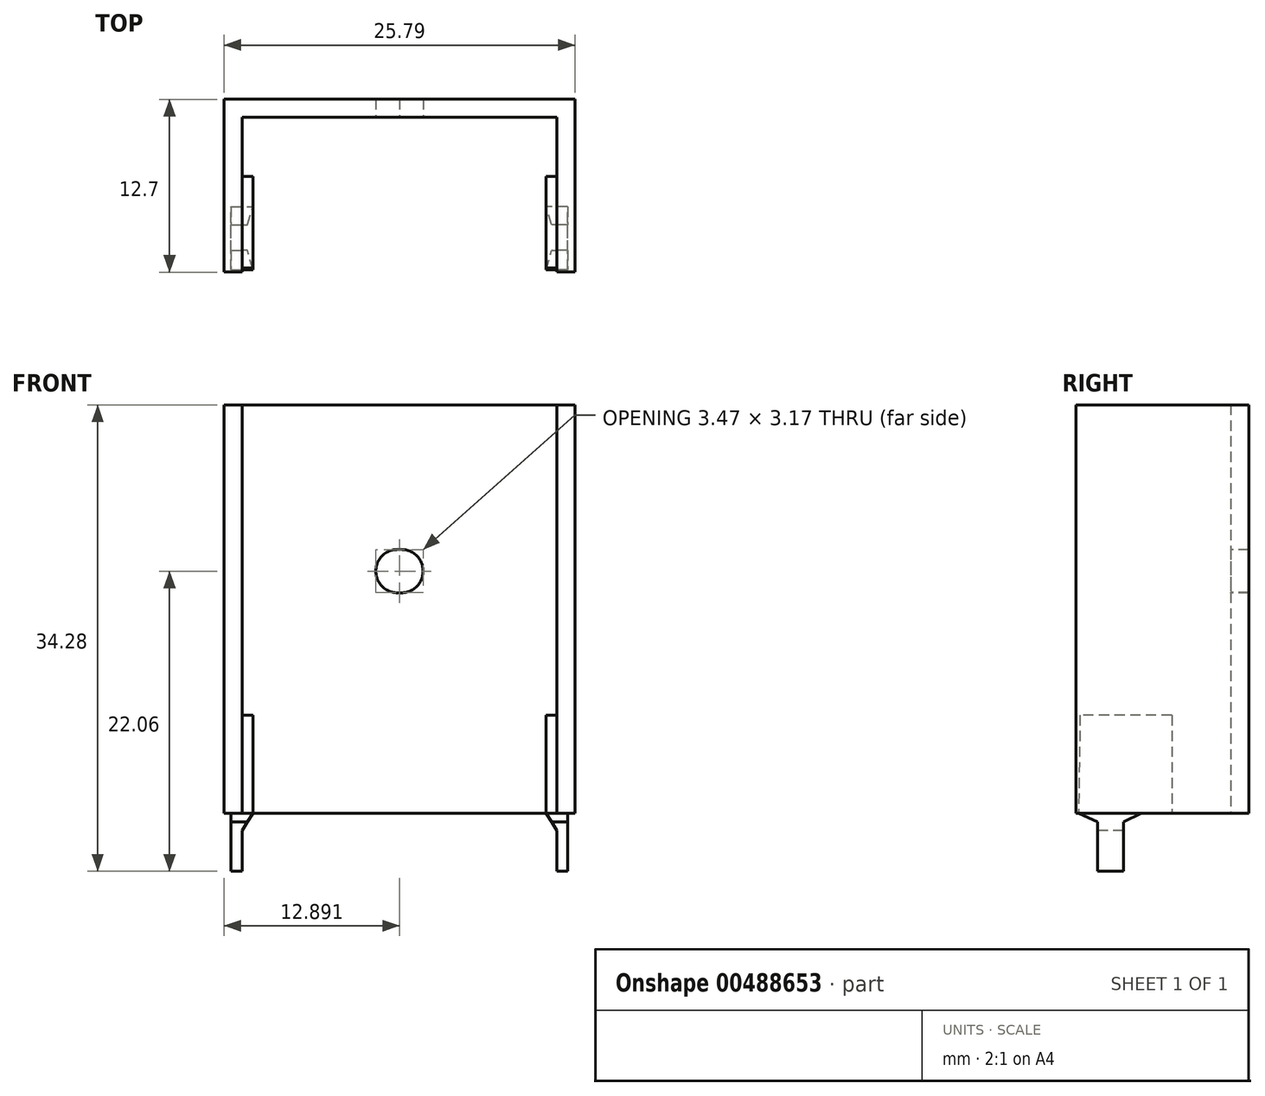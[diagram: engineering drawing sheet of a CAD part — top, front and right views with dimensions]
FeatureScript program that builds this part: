
annotation { "Feature Type Name" : "Feature", "Feature Type Description" : "" }
export const myFeature = defineFeature(function(context is Context, id is Id, definition is map)
    precondition{}
    {
        {
            var Q0;
            Q0=qCreatedBy(makeId("Top.planeOp"),FACE);
            var sketch = newSketch(context, id + "F0", { "sketchPlane" : qUnion([Q0])});
            skLineSegment(sketch, "E0", {"start": v(-6.3, -5.6) * mm, "end": v(-4.97, -5.6) * mm});
            skLineSegment(sketch, "E1", {"start": v(-4.97, -5.6) * mm, "end": v(-4.97, 5.77) * mm});
            skLineSegment(sketch, "E2", {"start": v(-6.3, 7.1) * mm, "end": v(-6.3, -5.6) * mm});
            skLineSegment(sketch, "E3", {"start": v(6.6, 7.1) * mm, "end": v(6.6, 5.77) * mm});
            skLineSegment(sketch, "E4", {"start": v(6.6, 7.1) * mm, "end": v(-6.3, 7.1) * mm});
            skLineSegment(sketch, "E5", {"start": v(-4.97, 5.77) * mm, "end": v(6.6, 5.77) * mm});
            skSolve(sketch);
        }
        {
            var Q0;
            Q0 = qSketchRegion(id + "F0", true);
            extrude(context, id + "F1", {"entities" : qUnion([Q0]), "depth" : 30 * mm});
        }
        {
            var Q0;
            Q0=makeQuery(id+"F1.opExtrude","SWEPT_FACE",FACE,{"disambiguationData":[OSD([sQuery(id+"F0.wireOp",EDGE,"E5")])]});
            var sketch = newSketch(context, id + "F2", { "sketchPlane" : qUnion([Q0])});
            skCircle(sketch, "E6", {"center": v(6.45, 17.78) * mm, "radius": 1.59 * mm});
            skSolve(sketch);
        }
        {
            var Q0;
            Q0 = qSketchRegion(id + "F2", true);
            extrude(context, id + "F3", {"entities" : qUnion([Q0]), "operationType" : NewBodyOperationType.REMOVE, "endBound" : BoundingType.THROUGH_ALL, "oppositeDirection" : true, "depth" : 25 * mm});
        }
        {
            var Q0;
            Q0=makeQuery(id+"F1.opExtrude","SWEPT_FACE",FACE,{"disambiguationData":[OSD([sQuery(id+"F0.wireOp",EDGE,"E1")])]});
            var sketch = newSketch(context, id + "F4", { "sketchPlane" : qUnion([Q0])});
            skLineSegment(sketch, "E7", {"start": v(-5.3, 7.19) * mm, "end": v(1.44, 7.19) * mm});
            skLineSegment(sketch, "E8", {"start": v(-4, -4.28) * mm, "end": v(-2.1, -4.27) * mm});
            skLineSegment(sketch, "E9", {"start": v(-0.79, 0) * mm, "end": v(1.44, 0) * mm});
            skLineSegment(sketch, "E10", {"start": v(1.44, 0) * mm, "end": v(1.44, 7.19) * mm});
            skLineSegment(sketch, "E11", {"start": v(-0.79, 0) * mm, "end": v(-2.1, -0.64) * mm});
            skLineSegment(sketch, "E12", {"start": v(-2.1, -0.64) * mm, "end": v(-2.1, -4.27) * mm});
            skLineSegment(sketch, "E13", {"start": v(-4, -4.28) * mm, "end": v(-4, -0.65) * mm});
            skLineSegment(sketch, "E14", {"start": v(-4, -0.65) * mm, "end": v(-5.4, 0) * mm});
            skLineSegment(sketch, "E15", {"start": v(-5.4, 0) * mm, "end": v(-5.3, 7.19) * mm});
            skSolve(sketch);
        }
        {
            var Q0;
            Q0 = qSketchRegion(id + "F4", true);
            extrude(context, id + "F5", {"entities" : qUnion([Q0]), "operationType" : NewBodyOperationType.ADD, "endBound" : BoundingType.SYMMETRIC, "oppositeDirection" : true, "depth" : 1.6 * mm});
        }
        {
            var Q0;
            Q0=makeQuery(id+"F5.opExtrude","SWEPT_FACE",FACE,{"disambiguationData":[OSD([sQuery(id+"F4.wireOp",EDGE,"E13")])]});
            var sketch = newSketch(context, id + "F6", { "sketchPlane" : qUnion([Q0])});
            skLineSegment(sketch, "E16", {"start": v(-4.97, -1.28) * mm, "end": v(-4.17, 0) * mm});
            skLineSegment(sketch, "E17", {"start": v(-4.17, 0) * mm, "end": v(-4.17, -4.28) * mm});
            skLineSegment(sketch, "E18", {"start": v(-4.17, -4.28) * mm, "end": v(-4.97, -4.28) * mm});
            skLineSegment(sketch, "E19", {"start": v(-4.97, -4.28) * mm, "end": v(-4.97, -1.28) * mm});
            skSolve(sketch);
        }
        {
            var Q0;
            Q0 = qSketchRegion(id + "F6", true);
            extrude(context, id + "F7", {"entities" : qUnion([Q0]), "operationType" : NewBodyOperationType.REMOVE, "endBound" : BoundingType.SYMMETRIC, "oppositeDirection" : true, "depth" : 1000 * mm});
        }
        {
            var Q0;
            Q0=makeQuery(id+"F1.opExtrude","SWEPT_BODY",BODY,{"disambiguationData":[OSD([sQuery(id+"F0.wireOp",EDGE,"E0"),sQuery(id+"F0.wireOp",EDGE,"E1"),sQuery(id+"F0.wireOp",EDGE,"E2"),sQuery(id+"F0.wireOp",EDGE,"E3"),sQuery(id+"F0.wireOp",EDGE,"E4"),sQuery(id+"F0.wireOp",EDGE,"E5")])]});
            var Q1;
            {var subQ0=sQuery(id+"F0.wireOp",EDGE,"E5");var subQ1=sQuery(id+"F0.wireOp",EDGE,"E4");var subQ2=sQuery(id+"F0.wireOp",EDGE,"E3");Q1=makeQuery(id+"F3.boolean.opBoolean","SPLIT",FACE,{"disambiguationData":[TD([makeQuery(id+"F1.opExtrude","CAP_FACE",FACE,{"disambiguationData":[OSD([sQuery(id+"F0.wireOp",EDGE,"E0"),sQuery(id+"F0.wireOp",EDGE,"E1"),sQuery(id+"F0.wireOp",EDGE,"E2"),subQ2,subQ1,subQ0])],"isStart":true})])],"derivedFrom":makeQuery(id+"F1.opExtrude","SWEPT_FACE",FACE,{"disambiguationData":[OSD([subQ2])]})});}
            mirror(context, id + "F8", {"operationType" : NewBodyOperationType.ADD, "entities" : qUnion([Q0]), "mirrorPlane" : qUnion([Q1])});
        }
    });
